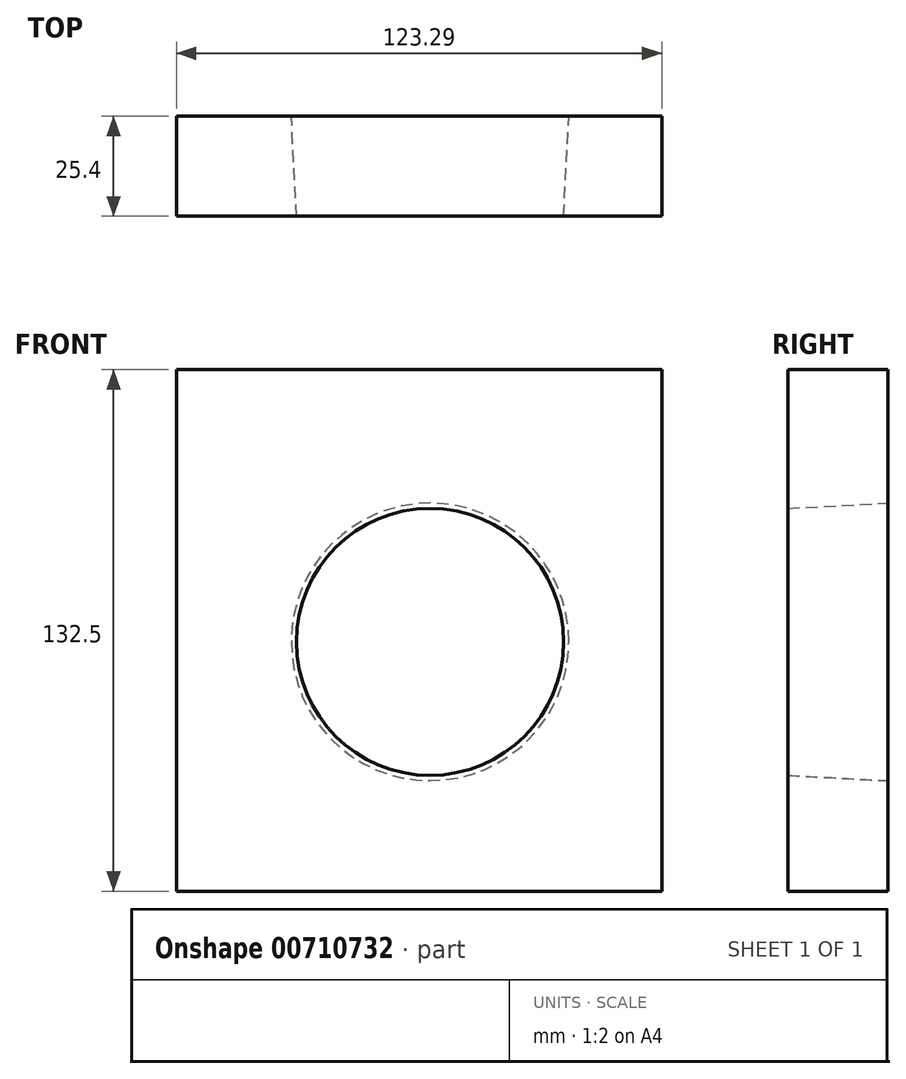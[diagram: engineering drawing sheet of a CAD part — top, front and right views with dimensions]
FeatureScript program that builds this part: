
annotation { "Feature Type Name" : "Feature", "Feature Type Description" : "" }
export const myFeature = defineFeature(function(context is Context, id is Id, definition is map)
    precondition{}
    {
        {
            var Q0;
            Q0=qCreatedBy(makeId("Front.planeOp"),FACE);
            var sketch = newSketch(context, id + "F0", { "sketchPlane" : qUnion([Q0])});
            skLineSegment(sketch, "E0.bottom", {"start": v(-100.67, 0) * mm, "end": v(-223.96, 0) * mm});
            skLineSegment(sketch, "E0.top", {"start": v(-100.67, -132.5) * mm, "end": v(-223.96, -132.5) * mm});
            skLineSegment(sketch, "E0.left", {"start": v(-100.67, 0) * mm, "end": v(-100.67, -132.5) * mm});
            skLineSegment(sketch, "E0.right", {"start": v(-223.96, 0) * mm, "end": v(-223.96, -132.5) * mm});
            skSolve(sketch);
        }
        {
            var Q0;
            Q0 = qSketchRegion(id + "F0", true);
            extrude(context, id + "F1", {"entities" : qUnion([Q0]), "depth" : 25.4 * mm, "offsetDistance" : 25.4 * mm});
        }
        {
            var Q0;
            Q0=makeQuery(id+"F1.opExtrude","CAP_FACE",FACE,{"disambiguationData":[OSD([sQuery(id+"F0.wireOp",EDGE,"E0.bottom"),sQuery(id+"F0.wireOp",EDGE,"E0.top"),sQuery(id+"F0.wireOp",EDGE,"E0.left"),sQuery(id+"F0.wireOp",EDGE,"E0.right")])],"isStart":false});
            var sketch = newSketch(context, id + "F2", { "sketchPlane" : qUnion([Q0])});
            skCircle(sketch, "E1", {"center": v(-159.53, -69.14) * mm, "radius": 33.93 * mm});
            skSolve(sketch);
        }
        {
            var Q0;
            Q0 = qSketchRegion(id + "F2", true);
            extrude(context, id + "F3", {"entities" : qUnion([Q0]), "operationType" : NewBodyOperationType.REMOVE, "oppositeDirection" : true, "depth" : 25.4 * mm, "offsetDistance" : 25.4 * mm, "hasDraft" : true, "draftAngle" : 3 * degree});
        }
    });
